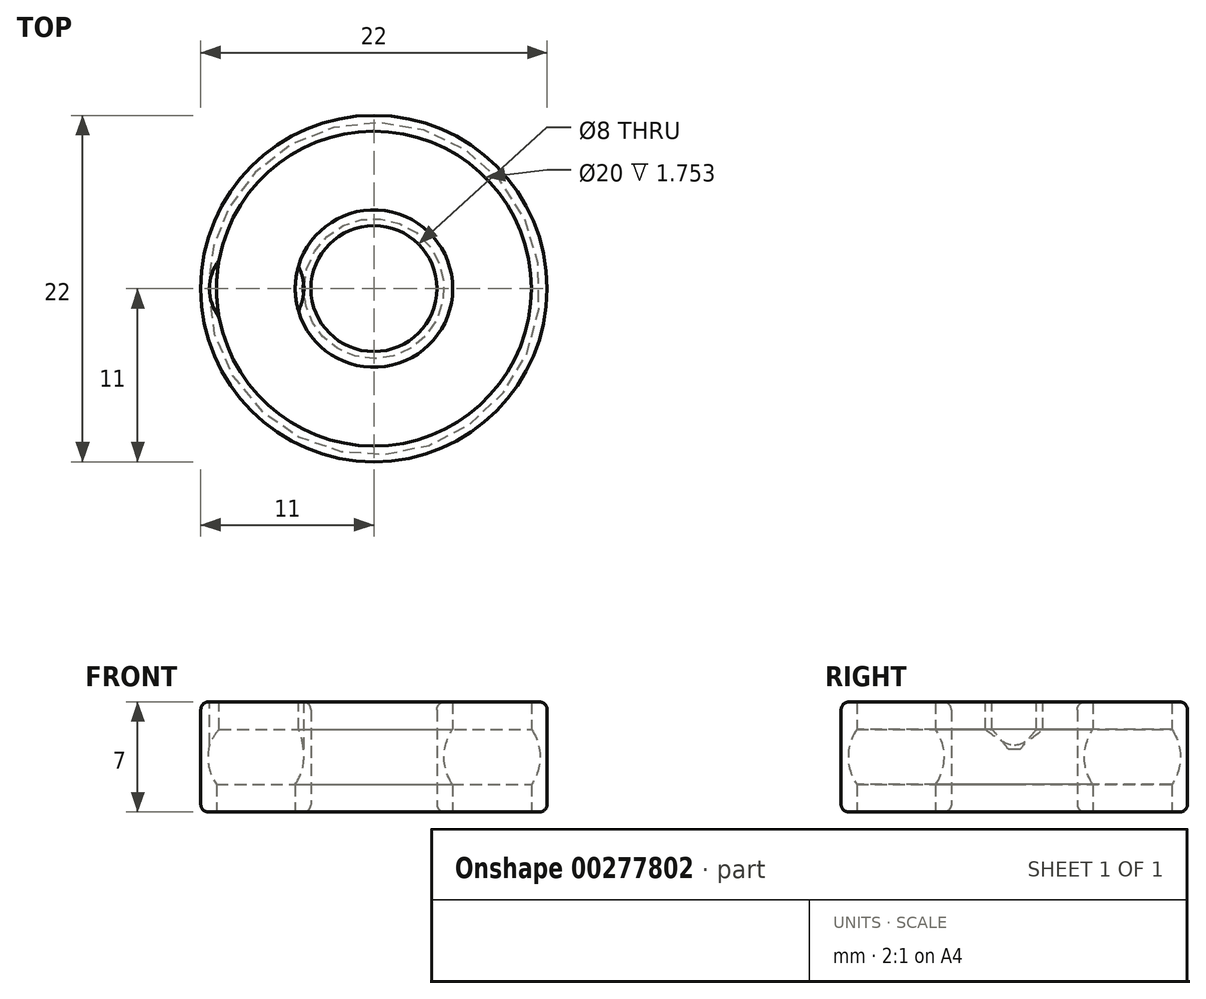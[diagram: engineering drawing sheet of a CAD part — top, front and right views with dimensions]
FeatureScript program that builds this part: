
annotation { "Feature Type Name" : "Feature", "Feature Type Description" : "" }
export const myFeature = defineFeature(function(context is Context, id is Id, definition is map)
    precondition{}
    {
        {
            var Q0;
            Q0=qCreatedBy(makeId("Front.planeOp"),FACE);
            var sketch = newSketch(context, id + "F0", { "sketchPlane" : qUnion([Q0])});
            skPoint(sketch, "E0.middle", {"position": v(0, 0) * mm});
            skLineSegment(sketch, "E1.bottom", {"start": v(0, 0) * mm, "end": v(-11, 0) * mm});
            skLineSegment(sketch, "E1.top", {"start": v(0, 7) * mm, "end": v(-11, 7) * mm});
            skLineSegment(sketch, "E1.left", {"start": v(0, 0) * mm, "end": v(0, 7) * mm});
            skLineSegment(sketch, "E1.right", {"start": v(-11, 0) * mm, "end": v(-11, 7) * mm});
            skPoint(sketch, "E2", {"position": v(-7.5, 3.5) * mm});
            skCircle(sketch, "E3", {"center": v(-7.5, 3.5) * mm, "radius": 3.05 * mm});
            skLineSegment(sketch, "E4", {"start": v(-4, 7) * mm, "end": v(-4, 0) * mm});
            skLineSegment(sketch, "E5.bottom", {"start": v(-5, 0) * mm, "end": v(-10, 0) * mm});
            skLineSegment(sketch, "E5.top", {"start": v(-5, 7) * mm, "end": v(-10, 7) * mm});
            skLineSegment(sketch, "E5.left", {"start": v(-5, 0) * mm, "end": v(-5, 7) * mm});
            skLineSegment(sketch, "E5.right", {"start": v(-10, 0) * mm, "end": v(-10, 7) * mm});
            skSolve(sketch);
        }
        {
            var Q0;
            {var subQ0=sQuery(id+"F0.wireOp",EDGE,"E1.right");Q0=makeQuery(id+"F0.imprint","IMPRINT",FACE,{"disambiguationData":[TD([[makeQuery(id+"F0.imprint","IMPRINT",EDGE,{"derivedFrom":subQ0}),-1.0]])]});}
            var Q1;
            {var subQ0=sQuery(id+"F0.wireOp",EDGE,"E4");Q1=makeQuery(id+"F0.imprint","IMPRINT",FACE,{"disambiguationData":[TD([[makeQuery(id+"F0.imprint","IMPRINT",EDGE,{"derivedFrom":subQ0}),-1.0]])]});}
            var Q2;
            Q2=sQuery(id+"F0.wireOp",EDGE,"E1.left");
            revolve(context, id + "F1", {"entities" : qUnion([Q0, Q1]), "axis" : qUnion([Q2]), "revolveType" : RevolveType.FULL});
        }
        {
            var Q0;
            {var subQ0=sQuery(id+"F0.wireOp",EDGE,"E1.top");Q0=makeQuery(id+"F1.opRevolve","SWEPT_FACE",FACE,{"disambiguationData":[OSD([subQ0]),TDD([makeQuery(id+"F0.imprint","IMPRINT",EDGE,{"disambiguationData":[TD([[makeQuery(id+"F0.imprint","INTERSECT",VERTEX,{"derivedFrom":[subQ0,sQuery(id+"F0.wireOp",EDGE,"E4")]}),-1.0]])],"derivedFrom":subQ0})])]});}
            var sketch = newSketch(context, id + "F2", { "sketchPlane" : qUnion([Q0])});
            skPoint(sketch, "E6", {"position": v(-7.45, 0) * mm});
            skCircle(sketch, "E7", {"center": v(-7.45, 0) * mm, "radius": 3 * mm});
            skSolve(sketch);
        }
        {
            var Q0;
            {var subQ0=sQuery(id+"F2.wireOp",EDGE,"E7");var subQ1=sQuery(id+"F0.wireOp",EDGE,"E3");var subQ2=sQuery(id+"F0.wireOp",EDGE,"E1.top");var subQ3=makeQuery(id+"F1.opRevolve","SWEPT_EDGE",EDGE,{"disambiguationData":[OSD([subQ2,subQ1]),TDD([makeQuery(id+"F0.imprint","INTERSECT",VERTEX,{"disambiguationData":[OD(0.0)],"derivedFrom":[subQ2,subQ1]})])]});var subQ4=makeQuery(id+"F2.imprint","INTERSECT",VERTEX,{"disambiguationData":[OD(0.0)],"derivedFrom":[subQ3,subQ0]});Q0=makeQuery(id+"F2.imprint","IMPRINT",FACE,{"disambiguationData":[TD([[makeQuery(id+"F2.imprint","IMPRINT",EDGE,{"disambiguationData":[TD([[subQ4,1.0]])],"derivedFrom":subQ0}),1.0]])]});}
            extrude(context, id + "F3", {"entities" : qUnion([Q0]), "operationType" : NewBodyOperationType.REMOVE, "oppositeDirection" : true, "depth" : 3 * mm});
        }
        {
            var Q0;
            Q0 = qSketchRegion(id + "F2", true);
            extrude(context, id + "F4", {"entities" : qUnion([Q0]), "operationType" : NewBodyOperationType.REMOVE, "oppositeDirection" : true, "depth" : 3 * mm});
        }
        {
            var Q0;
            Q0=makeQuery(id+"F1.opRevolve","SWEPT_EDGE",EDGE,{"disambiguationData":[OSD([sQuery(id+"F0.wireOp",EDGE,"E1.top"),sQuery(id+"F0.wireOp",EDGE,"E1.right")])]});
            var Q1;
            Q1=makeQuery(id+"F1.opRevolve","SWEPT_EDGE",EDGE,{"disambiguationData":[OSD([sQuery(id+"F0.wireOp",EDGE,"E1.top"),sQuery(id+"F0.wireOp",EDGE,"E4")])]});
            var Q2;
            Q2=makeQuery(id+"F1.opRevolve","SWEPT_EDGE",EDGE,{"disambiguationData":[OSD([sQuery(id+"F0.wireOp",EDGE,"E1.bottom"),sQuery(id+"F0.wireOp",EDGE,"E4")])]});
            var Q3;
            Q3=makeQuery(id+"F1.opRevolve","SWEPT_EDGE",EDGE,{"disambiguationData":[OSD([sQuery(id+"F0.wireOp",EDGE,"E1.bottom"),sQuery(id+"F0.wireOp",EDGE,"E1.right")])]});
            fillet(context, id + "F5", {"entities" : qUnion([Q0, Q1, Q2, Q3]), "radius" : 0.5 * mm, "tangentPropagation" : true, "allowEdgeOverflow" : false});
        }
    });
